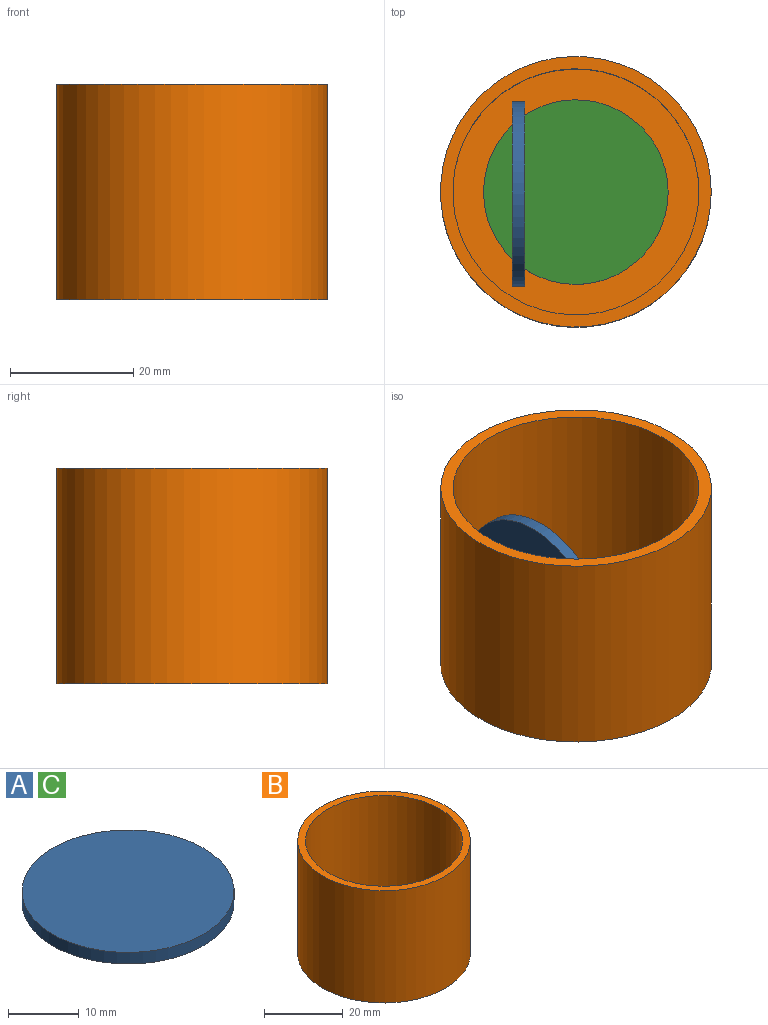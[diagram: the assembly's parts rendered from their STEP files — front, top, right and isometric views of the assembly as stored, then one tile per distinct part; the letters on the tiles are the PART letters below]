
ASSEMBLY  parts=3 mates=1
PART A: 3 faces, bbox 30x30x2 mm
  f0: cylinder r=15mm len=30mm, axis (0,0,1), area 188.5mm2, adj f1,f2
  f1: plane 30x30mm, normal (0,0,-1), area 706.9mm2, adj f0
  f2: plane 30x30mm, normal (0,0,1), area 706.9mm2, adj f0
PART B: 14 faces, bbox 44x44x35 mm
  f0: plane 11x11mm, normal (0,0,1), area 91.9mm2, adj f9,f11
  f1: cylinder r=20mm len=40mm, axis (0,0,-1), area 4146.9mm2, adj f3,f10
  f2: cylinder r=22mm len=44mm, axis (0,0,-1), area 4838.1mm2, adj f3,f4
  f3: plane 44x44mm, normal (0,0,1), area 263.9mm2, adj f1,f2
  f4: plane 44x44mm, normal (0,0,-1), area 1504.8mm2, adj f2,f5,f6,f7,f8,f9
  f5: cylinder r=1mm len=2mm, axis (0,0,-1), area 12.6mm2, adj f4,f10
  f6: cylinder r=1mm len=2mm, axis (0,0,-1), area 12.6mm2, adj f4,f10
  f7: cylinder r=1mm len=2mm, axis (0,0,-1), area 12.6mm2, adj f4,f10
  f8: cylinder r=1mm len=2mm, axis (0,0,-1), area 12.6mm2, adj f4,f10
  f9: cylinder r=1mm len=2mm, axis (0,0,-1), area 12.6mm2, adj f0,f4
  f10: plane 40x40mm, normal (0,0,1), area 1067.4mm2, adj f1,f5,f6,f7,f8,f12
  f11: cylinder r=5.5mm len=11mm, axis (0,0,-1), area 207.3mm2, adj f0,f13
  f12: cylinder r=7.5mm len=15mm, axis (0,0,-1), area 282.7mm2, adj f10,f13
  f13: plane 15x15mm, normal (0,0,1), area 81.7mm2, adj f11,f12
PART C: same geometry as A
PLACE A rot(axis=(0,-1,0),90deg) t=(-20.61,1.01,10.72)mm
PLACE B t=(-10.28,1.37,-6.54)mm fixed
PLACE C t=(-10.28,1.37,3.46)mm
MATE fastened B.f11 <-> C.f0  axis (0,0,1) through (-10.28,1.37,1.46)mm
